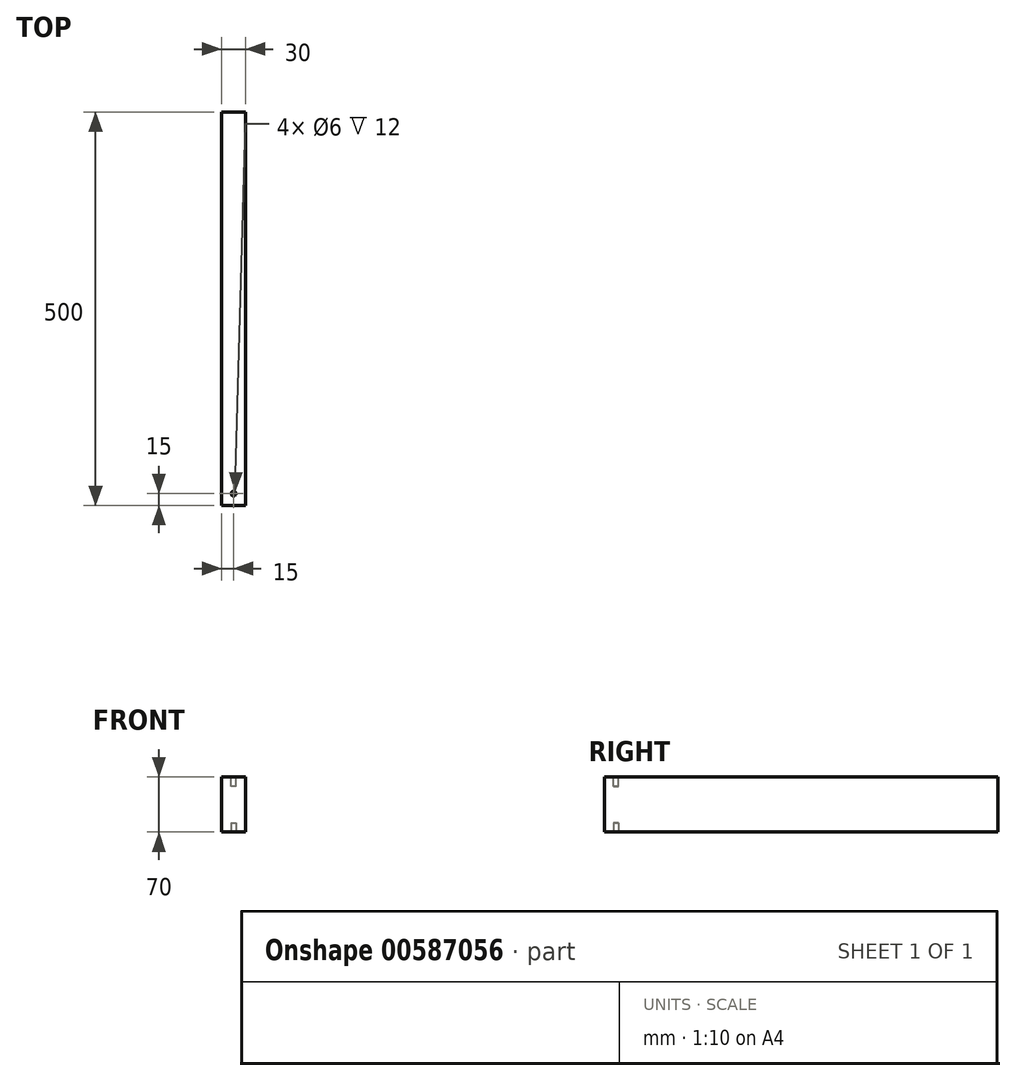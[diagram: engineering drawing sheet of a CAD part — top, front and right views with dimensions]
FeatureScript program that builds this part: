
annotation { "Feature Type Name" : "Feature", "Feature Type Description" : "" }
export const myFeature = defineFeature(function(context is Context, id is Id, definition is map)
    precondition{}
    {
        {
            var Q0;
            Q0=qCreatedBy(makeId("Right.planeOp"),FACE);
            var sketch = newSketch(context, id + "F0", { "sketchPlane" : qUnion([Q0])});
            skLineSegment(sketch, "E0.bottom", {"start": v(0, -1.24) * mm, "end": v(500, -1.24) * mm});
            skLineSegment(sketch, "E0.top", {"start": v(0, 68.76) * mm, "end": v(500, 68.76) * mm});
            skLineSegment(sketch, "E0.left", {"start": v(0, -1.24) * mm, "end": v(0, 68.76) * mm});
            skLineSegment(sketch, "E0.right", {"start": v(500, -1.24) * mm, "end": v(500, 68.76) * mm});
            skSolve(sketch);
        }
        {
            var Q0;
            Q0=makeQuery(id+"F0.imprint","IMPRINT",FACE,{"disambiguationData":[TD([[makeQuery(id+"F0.imprint","IMPRINT",EDGE,{"derivedFrom":sQuery(id+"F0.wireOp",EDGE,"E0.bottom")}),1.0]])]});
            extrude(context, id + "F1", {"entities" : qUnion([Q0]), "depth" : 30 * mm, "offsetDistance" : 25 * mm});
        }
        {
            var Q0;
            Q0=makeQuery(id+"F1.opExtrude","SWEPT_FACE",FACE,{"disambiguationData":[OSD([sQuery(id+"F0.wireOp",EDGE,"E0.top")])]});
            var sketch = newSketch(context, id + "F2", { "sketchPlane" : qUnion([Q0])});
            skCircle(sketch, "E1", {"center": v(15, 15) * mm, "radius": 3 * mm});
            skPoint(sketch, "E1.centerSnap0", {"position": v(15, 0) * mm});
            skSolve(sketch);
        }
        {
            var Q0;
            Q0=makeQuery(id+"F2.imprint","IMPRINT",FACE,{"disambiguationData":[TD([[makeQuery(id+"F2.imprint","IMPRINT",EDGE,{"derivedFrom":sQuery(id+"F2.wireOp",EDGE,"E1")}),1.0]])]});
            extrude(context, id + "F3", {"entities" : qUnion([Q0]), "operationType" : NewBodyOperationType.REMOVE, "oppositeDirection" : true, "depth" : 12 * mm, "offsetDistance" : 25 * mm});
        }
        {
            var Q0;
            Q0=makeQuery(id+"F1.opExtrude","SWEPT_FACE",FACE,{"disambiguationData":[OSD([sQuery(id+"F0.wireOp",EDGE,"E0.bottom")])]});
            var sketch = newSketch(context, id + "F4", { "sketchPlane" : qUnion([Q0])});
            skCircle(sketch, "E2.0", {"center": v(15, -15) * mm, "radius": 3 * mm});
            skSolve(sketch);
        }
        {
            var Q0;
            Q0=makeQuery(id+"F4.imprint","IMPRINT",FACE,{"disambiguationData":[TD([[makeQuery(id+"F4.imprint","IMPRINT",EDGE,{"derivedFrom":sQuery(id+"F4.wireOp",EDGE,"E2.0")}),1.0]])]});
            extrude(context, id + "F5", {"entities" : qUnion([Q0]), "operationType" : NewBodyOperationType.REMOVE, "oppositeDirection" : true, "depth" : 12 * mm, "offsetDistance" : 25 * mm});
        }
    });
